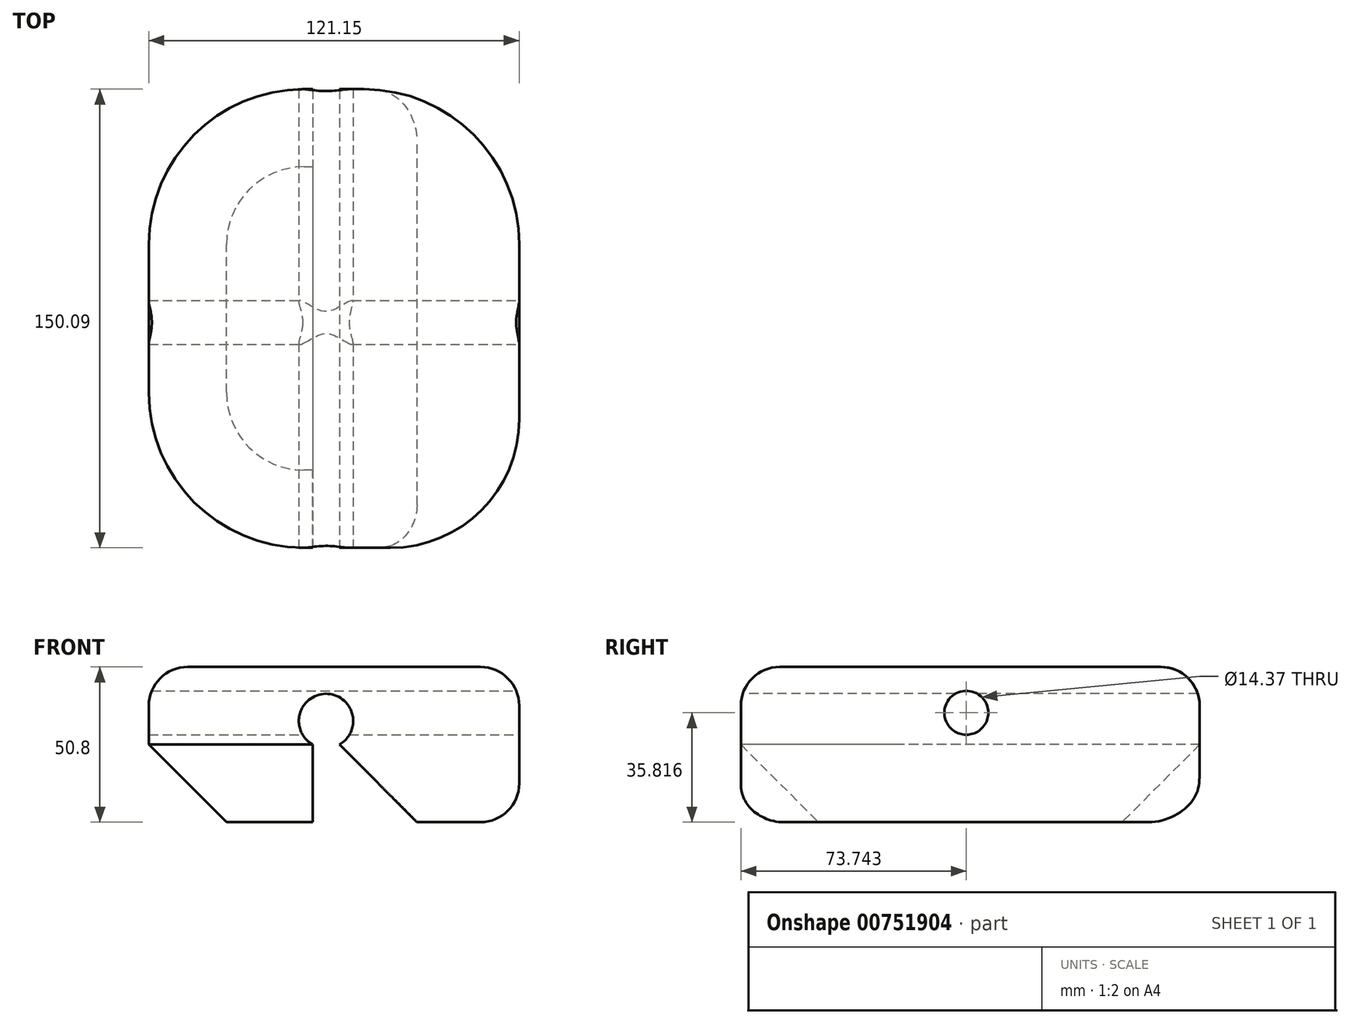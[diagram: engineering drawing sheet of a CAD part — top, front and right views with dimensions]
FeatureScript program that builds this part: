
annotation { "Feature Type Name" : "Feature", "Feature Type Description" : "" }
export const myFeature = defineFeature(function(context is Context, id is Id, definition is map)
    precondition{}
    {
        {
            var Q0;
            Q0=qCreatedBy(makeId("Top.planeOp"),FACE);
            var sketch = newSketch(context, id + "F0", { "sketchPlane" : qUnion([Q0])});
            skLineSegment(sketch, "E0.bottom", {"start": v(0, 0) * mm, "end": v(-121.15, 0) * mm});
            skLineSegment(sketch, "E0.top", {"start": v(0, 150.1) * mm, "end": v(-121.15, 150.1) * mm});
            skLineSegment(sketch, "E0.left", {"start": v(0, 0) * mm, "end": v(0, 150.1) * mm});
            skLineSegment(sketch, "E0.right", {"start": v(-121.15, 0) * mm, "end": v(-121.15, 150.1) * mm});
            skSolve(sketch);
        }
        {
            var Q0;
            Q0=makeQuery(id+"F0.imprint","IMPRINT",FACE,{"disambiguationData":[TD([[makeQuery(id+"F0.imprint","IMPRINT",EDGE,{"derivedFrom":sQuery(id+"F0.wireOp",EDGE,"E0.bottom")}),-1.0]])]});
            extrude(context, id + "F1", {"entities" : qUnion([Q0]), "depth" : 25.4 * mm, "offsetDistance" : 25.4 * mm});
        }
        {
            var Q0;
            Q0=makeQuery(id+"F1.opExtrude","SWEPT_FACE",FACE,{"disambiguationData":[OSD([sQuery(id+"F0.wireOp",EDGE,"E0.bottom")])]});
            var sketch = newSketch(context, id + "F2", { "sketchPlane" : qUnion([Q0])});
            skCircle(sketch, "E1", {"center": v(-63.19, 7.74) * mm, "radius": 8.89 * mm});
            skSolve(sketch);
        }
        {
            var Q0;
            {var subQ0=sQuery(id+"F2.wireOp",EDGE,"E1");var subQ1=makeQuery(id+"F1.opExtrude","CAP_EDGE",EDGE,{"disambiguationData":[OSD([sQuery(id+"F0.wireOp",EDGE,"E0.bottom")])],"isStart":true});var subQ2=makeQuery(id+"F2.imprint","INTERSECT",VERTEX,{"disambiguationData":[OD(0.0)],"derivedFrom":[subQ1,subQ0]});Q0=makeQuery(id+"F2.imprint","IMPRINT",FACE,{"disambiguationData":[TD([[makeQuery(id+"F2.imprint","IMPRINT",EDGE,{"disambiguationData":[TD([[subQ2,-1.0]])],"derivedFrom":subQ0}),1.0]])]});}
            extrude(context, id + "F3", {"entities" : qUnion([Q0]), "operationType" : NewBodyOperationType.REMOVE, "oppositeDirection" : true, "depth" : 226.57 * mm, "offsetDistance" : 25.4 * mm});
        }
        {
            var Q0;
            Q0=makeQuery(id+"F1.opExtrude","SWEPT_FACE",FACE,{"disambiguationData":[OSD([sQuery(id+"F0.wireOp",EDGE,"E0.left")])]});
            var sketch = newSketch(context, id + "F4", { "sketchPlane" : qUnion([Q0])});
            skCircle(sketch, "E2", {"center": v(73.74, 10.42) * mm, "radius": 7.18 * mm});
            skSolve(sketch);
        }
        {
            var Q0;
            Q0=makeQuery(id+"F4.imprint","IMPRINT",FACE,{"disambiguationData":[TD([[makeQuery(id+"F4.imprint","IMPRINT",EDGE,{"derivedFrom":sQuery(id+"F4.wireOp",EDGE,"E2")}),1.0]])]});
            extrude(context, id + "F5", {"entities" : qUnion([Q0]), "operationType" : NewBodyOperationType.REMOVE, "oppositeDirection" : true, "depth" : 171.9 * mm, "offsetDistance" : 25.4 * mm});
        }
        {
            var Q0;
            Q0=makeQuery(id+"F1.opExtrude","SWEPT_EDGE",EDGE,{"disambiguationData":[OSD([sQuery(id+"F0.wireOp",EDGE,"E0.bottom"),sQuery(id+"F0.wireOp",EDGE,"E0.left")])]});
            fillet(context, id + "F6", {"entities" : qUnion([Q0]), "radius" : 42.13 * mm, "tangentPropagation" : true, "allowEdgeOverflow" : false});
        }
        {
            var Q0;
            Q0=makeQuery(id+"F1.opExtrude","SWEPT_EDGE",EDGE,{"disambiguationData":[OSD([sQuery(id+"F0.wireOp",EDGE,"E0.top"),sQuery(id+"F0.wireOp",EDGE,"E0.left")])]});
            fillet(context, id + "F7", {"entities" : qUnion([Q0]), "radius" : 50.8 * mm, "tangentPropagation" : true, "allowEdgeOverflow" : false});
        }
        {
            var Q0;
            Q0=makeQuery(id+"F1.opExtrude","SWEPT_EDGE",EDGE,{"disambiguationData":[OSD([sQuery(id+"F0.wireOp",EDGE,"E0.bottom"),sQuery(id+"F0.wireOp",EDGE,"E0.right")])]});
            fillet(context, id + "F8", {"entities" : qUnion([Q0]), "radius" : 50.8 * mm, "tangentPropagation" : true, "allowEdgeOverflow" : false});
        }
        {
            var Q0;
            Q0=makeQuery(id+"F1.opExtrude","SWEPT_EDGE",EDGE,{"disambiguationData":[OSD([sQuery(id+"F0.wireOp",EDGE,"E0.top"),sQuery(id+"F0.wireOp",EDGE,"E0.right")])]});
            fillet(context, id + "F9", {"entities" : qUnion([Q0]), "radius" : 50.8 * mm, "tangentPropagation" : true, "allowEdgeOverflow" : false});
        }
        {
            var Q0;
            {var subQ0=sQuery(id+"F0.wireOp",EDGE,"E0.bottom");var subQ1=sQuery(id+"F0.wireOp",EDGE,"E0.top");var subQ2=sQuery(id+"F0.wireOp",EDGE,"E0.left");Q0=makeQuery(id+"F3.boolean.opBoolean","SPLIT",FACE,{"disambiguationData":[TD([makeQuery(id+"F1.opExtrude","SWEPT_FACE",FACE,{"disambiguationData":[OSD([subQ2])]})])],"derivedFrom":makeQuery(id+"F1.opExtrude","CAP_FACE",FACE,{"disambiguationData":[OSD([subQ0,subQ1,subQ2,sQuery(id+"F0.wireOp",EDGE,"E0.right")])],"isStart":true})});}
            extrude(context, id + "F10", {"entities" : qUnion([Q0]), "operationType" : NewBodyOperationType.ADD, "depth" : 25.4 * mm, "offsetDistance" : 25.4 * mm});
        }
        {
            var Q0;
            {var subQ0=sQuery(id+"F0.wireOp",EDGE,"E0.bottom");var subQ1=sQuery(id+"F0.wireOp",EDGE,"E0.right");var subQ2=sQuery(id+"F0.wireOp",EDGE,"E0.top");Q0=makeQuery(id+"F3.boolean.opBoolean","SPLIT",FACE,{"disambiguationData":[TD([makeQuery(id+"F1.opExtrude","SWEPT_FACE",FACE,{"disambiguationData":[OSD([subQ1])]})])],"derivedFrom":makeQuery(id+"F1.opExtrude","CAP_FACE",FACE,{"disambiguationData":[OSD([subQ0,subQ2,sQuery(id+"F0.wireOp",EDGE,"E0.left"),subQ1])],"isStart":true})});}
            extrude(context, id + "F11", {"entities" : qUnion([Q0]), "operationType" : NewBodyOperationType.ADD, "depth" : 25.4 * mm, "offsetDistance" : 25.4 * mm});
        }
        {
            var Q0;
            Q0=makeQuery(id+"F10.opExtrude","CAP_EDGE",EDGE,{"disambiguationData":[OSD([sQuery(id+"F0.wireOp",EDGE,"E0.bottom"),sQuery(id+"F2.wireOp",EDGE,"E1")])],"isStart":false});
            chamfer(context, id + "F12", {"entities" : qUnion([Q0]), "width" : 25.4 * mm, "tangentPropagation" : true});
        }
        {
            var Q0;
            Q0=makeQuery(id+"F11.opExtrude","CAP_EDGE",EDGE,{"disambiguationData":[OSD([sQuery(id+"F0.wireOp",EDGE,"E0.bottom"),sQuery(id+"F2.wireOp",EDGE,"E1")])],"isStart":false});
            chamfer(context, id + "F13", {"entities" : qUnion([Q0]), "width" : 25.4 * mm, "tangentPropagation" : true});
        }
        {
            var Q0;
            {var subQ0=sQuery(id+"F0.wireOp",EDGE,"E0.right");var subQ1=sQuery(id+"F0.wireOp",EDGE,"E0.bottom");Q0=makeQuery(id+"F8.opFillet","BLEND_EDGE",EDGE,{"blendedFrom":[makeQuery(id+"F1.opExtrude","SWEPT_EDGE",EDGE,{"disambiguationData":[OSD([subQ1,subQ0])]}),makeQuery(id+"F1.opExtrude","CAP_FACE",FACE,{"disambiguationData":[OSD([subQ1,sQuery(id+"F0.wireOp",EDGE,"E0.top"),sQuery(id+"F0.wireOp",EDGE,"E0.left"),subQ0])],"isStart":false})],"blendedInto":[makeQuery(id+"F1.opExtrude","CAP_FACE",FACE,{"disambiguationData":[OSD([subQ1,sQuery(id+"F0.wireOp",EDGE,"E0.top"),sQuery(id+"F0.wireOp",EDGE,"E0.left"),subQ0])],"isStart":false})]});}
            fillet(context, id + "F14", {"entities" : qUnion([Q0]), "radius" : 12.7 * mm, "tangentPropagation" : true, "allowEdgeOverflow" : false});
        }
        {
            var Q0;
            {var subQ0=sQuery(id+"F0.wireOp",EDGE,"E0.bottom");var subQ1=sQuery(id+"F0.wireOp",EDGE,"E0.top");var subQ2=sQuery(id+"F0.wireOp",EDGE,"E0.left");var subQ3=sQuery(id+"F0.wireOp",EDGE,"E0.right");Q0=makeQuery(id+"F10.opExtrude","CAP_EDGE",EDGE,{"disambiguationData":[OSD([subQ0,subQ1,subQ2,subQ3]),TDD([makeQuery(id+"F7.opFillet","BLEND_EDGE",EDGE,{"blendedFrom":[makeQuery(id+"F1.opExtrude","SWEPT_EDGE",EDGE,{"disambiguationData":[OSD([subQ1,subQ2])]}),makeQuery(id+"F3.boolean.opBoolean","SPLIT",FACE,{"disambiguationData":[TD([makeQuery(id+"F1.opExtrude","SWEPT_FACE",FACE,{"disambiguationData":[OSD([subQ2])]})])],"derivedFrom":makeQuery(id+"F1.opExtrude","CAP_FACE",FACE,{"disambiguationData":[OSD([subQ0,subQ1,subQ2,subQ3])],"isStart":true})})],"blendedInto":[makeQuery(id+"F3.boolean.opBoolean","SPLIT",FACE,{"disambiguationData":[TD([makeQuery(id+"F1.opExtrude","SWEPT_FACE",FACE,{"disambiguationData":[OSD([subQ2])]})])],"derivedFrom":makeQuery(id+"F1.opExtrude","CAP_FACE",FACE,{"disambiguationData":[OSD([subQ0,subQ1,subQ2,subQ3])],"isStart":true})})]})])],"isStart":false});}
            fillet(context, id + "F15", {"entities" : qUnion([Q0]), "radius" : 12.7 * mm, "tangentPropagation" : true, "allowEdgeOverflow" : false});
        }
    });
